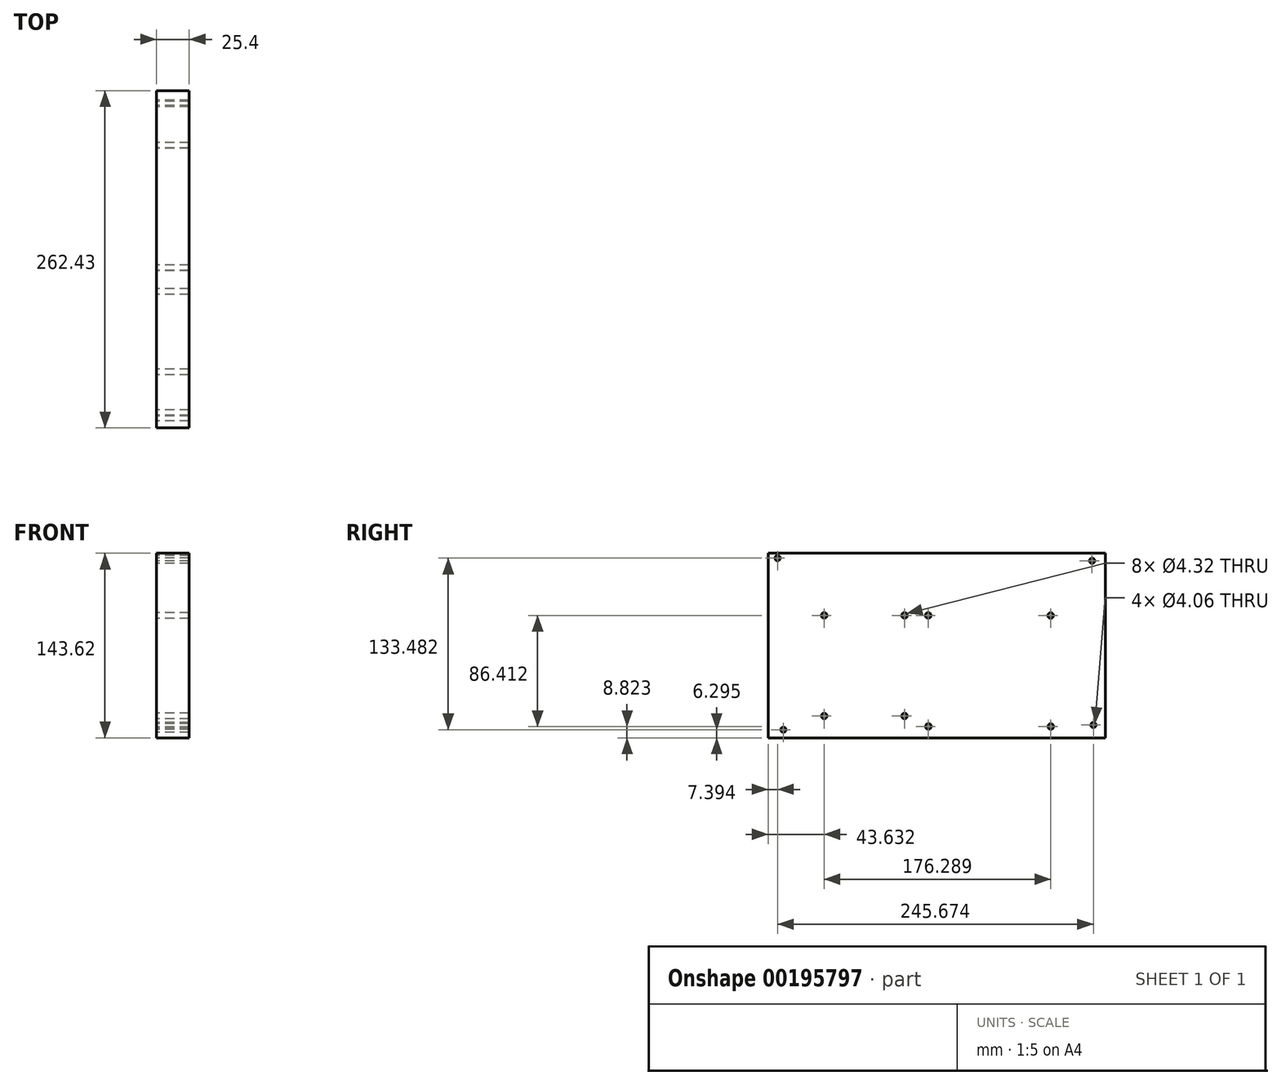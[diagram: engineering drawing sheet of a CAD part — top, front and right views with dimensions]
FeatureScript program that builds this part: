
annotation { "Feature Type Name" : "Feature", "Feature Type Description" : "" }
export const myFeature = defineFeature(function(context is Context, id is Id, definition is map)
    precondition{}
    {
        {
            var Q0;
            Q0=qCreatedBy(makeId("Right.planeOp"),FACE);
            var sketch = newSketch(context, id + "F0", { "sketchPlane" : qUnion([Q0])});
            skCircle(sketch, "E0", {"center": v(-70.14, 62.5) * mm, "radius": 2.03 * mm});
            skCircle(sketch, "E1", {"center": v(-33.9, 17.95) * mm, "radius": 2.16 * mm});
            skCircle(sketch, "E2", {"center": v(28.59, 17.95) * mm, "radius": 2.16 * mm});
            skCircle(sketch, "E3", {"center": v(28.57, -60.28) * mm, "radius": 2.16 * mm});
            skCircle(sketch, "E4", {"center": v(-33.9, -60.28) * mm, "radius": 2.16 * mm});
            skCircle(sketch, "E5", {"center": v(142.3, 17.9) * mm, "radius": 2.16 * mm});
            skCircle(sketch, "E6", {"center": v(47.04, 17.94) * mm, "radius": 2.16 * mm});
            skCircle(sketch, "E7", {"center": v(142.4, -68.46) * mm, "radius": 2.16 * mm});
            skCircle(sketch, "E8", {"center": v(47.14, -68.42) * mm, "radius": 2.16 * mm});
            skCircle(sketch, "E9", {"center": v(175.54, -67.3) * mm, "radius": 2.03 * mm});
            skCircle(sketch, "E10", {"center": v(174.52, 60.5) * mm, "radius": 2.03 * mm});
            skCircle(sketch, "E11", {"center": v(-65.66, -70.98) * mm, "radius": 2.03 * mm});
            skLineSegment(sketch, "E12.bottom", {"start": v(184.9, 66.34) * mm, "end": v(-77.53, 66.34) * mm});
            skLineSegment(sketch, "E12.top", {"start": v(184.9, -77.28) * mm, "end": v(-77.53, -77.28) * mm});
            skLineSegment(sketch, "E12.left", {"start": v(184.9, 66.34) * mm, "end": v(184.9, -77.28) * mm});
            skLineSegment(sketch, "E12.right", {"start": v(-77.53, 66.34) * mm, "end": v(-77.53, -77.28) * mm});
            skSolve(sketch);
        }
        {
            var Q0;
            Q0 = qSketchRegion(id + "F0", true);
            extrude(context, id + "F1", {"entities" : qUnion([Q0]), "depth" : 25.4 * mm});
        }
    });
